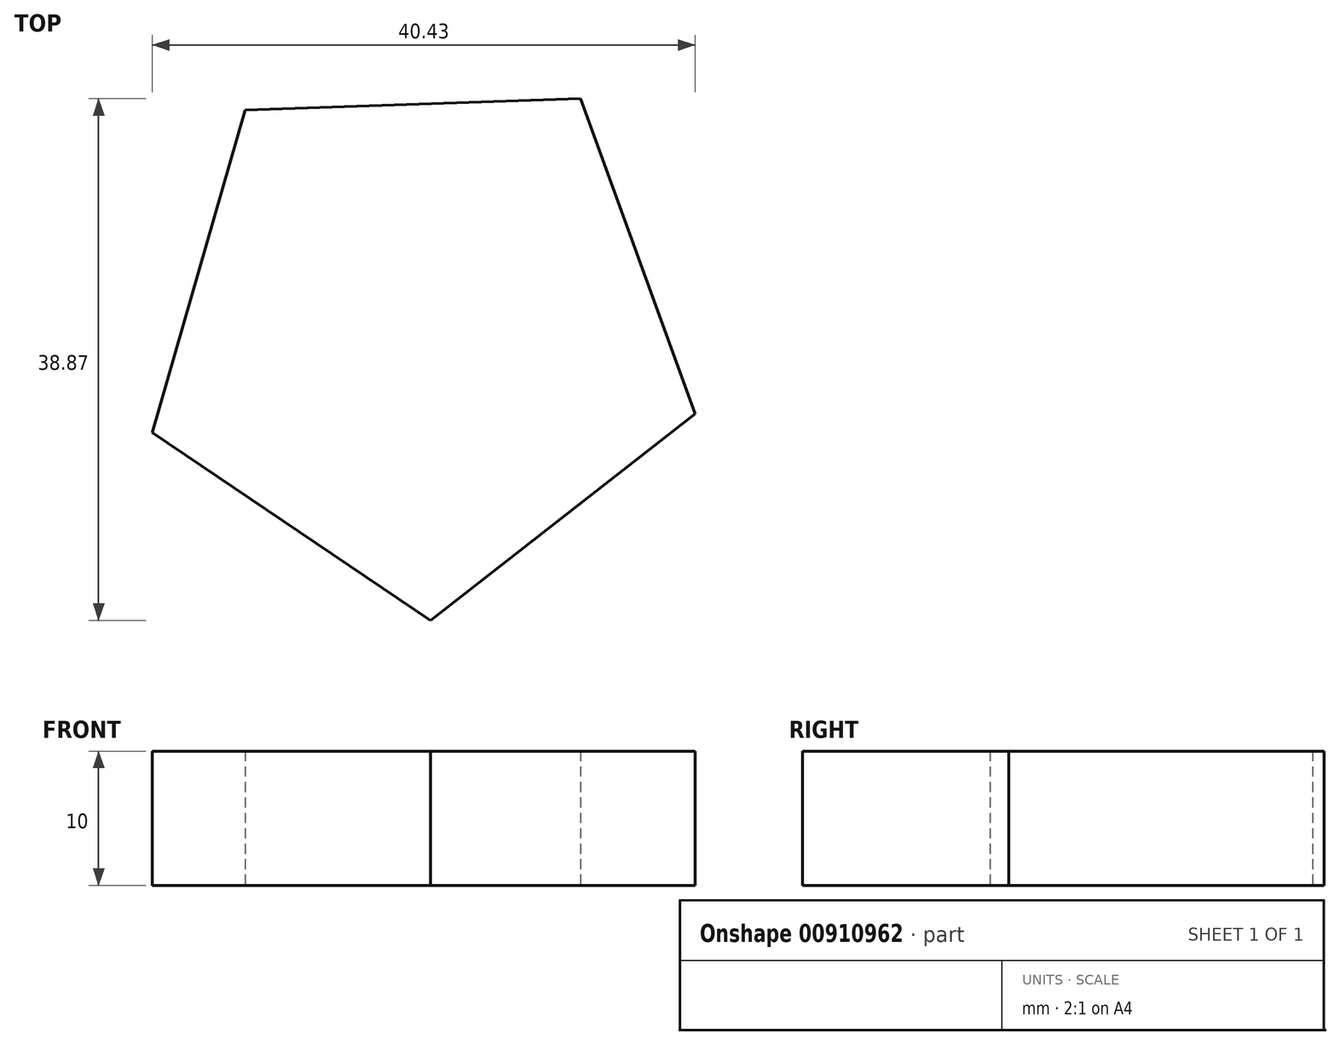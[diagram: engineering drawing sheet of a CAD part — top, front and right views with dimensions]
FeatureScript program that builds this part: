
annotation { "Feature Type Name" : "Feature", "Feature Type Description" : "" }
export const myFeature = defineFeature(function(context is Context, id is Id, definition is map)
    precondition{}
    {
        {
            var Q0;
            Q0=qCreatedBy(makeId("Top.planeOp"),FACE);
            var sketch = newSketch(context, id + "F0", { "sketchPlane" : qUnion([Q0])});
            skCircle(sketch, "E0.cCircle", {"center": v(0, 0) * mm, "radius": 17.2 * mm, "construction": true});
            skLineSegment(sketch, "E0.0", {"start": v(20.44, -5.88) * mm, "end": v(0.72, -21.25) * mm});
            skLineSegment(sketch, "E0.1", {"start": v(0.72, -21.25) * mm, "end": v(-19.99, -7.26) * mm});
            skLineSegment(sketch, "E0.2", {"start": v(-19.99, -7.26) * mm, "end": v(-13.08, 16.77) * mm});
            skLineSegment(sketch, "E0.3", {"start": v(-13.08, 16.77) * mm, "end": v(11.9, 17.62) * mm});
            skLineSegment(sketch, "E0.4", {"start": v(11.9, 17.62) * mm, "end": v(20.44, -5.88) * mm});
            skPoint(sketch, "E0.0.midPoint", {"position": v(10.58, -13.57) * mm});
            skSolve(sketch);
        }
        {
            var Q0;
            Q0=makeQuery(id+"F0.imprint","IMPRINT",FACE,{"disambiguationData":[TD([[makeQuery(id+"F0.imprint","IMPRINT",EDGE,{"derivedFrom":sQuery(id+"F0.wireOp",EDGE,"E0.0")}),-1.0]])]});
            extrude(context, id + "F1", {"entities" : qUnion([Q0]), "depth" : 10 * mm, "offsetDistance" : 25 * mm});
        }
    });
